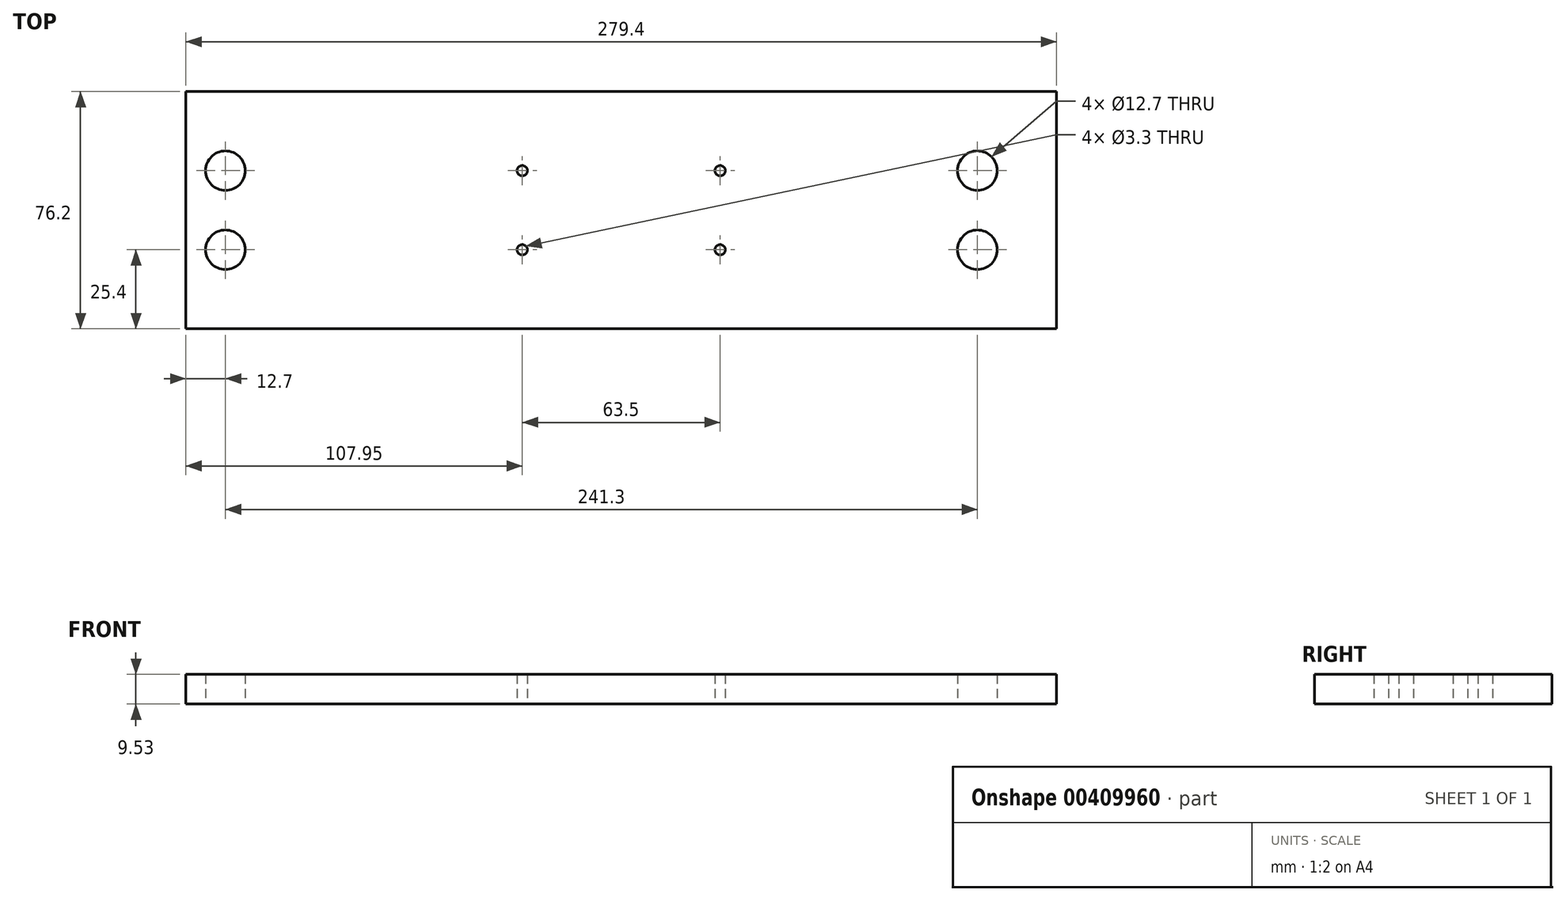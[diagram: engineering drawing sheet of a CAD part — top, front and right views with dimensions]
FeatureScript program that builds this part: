
annotation { "Feature Type Name" : "Feature", "Feature Type Description" : "" }
export const myFeature = defineFeature(function(context is Context, id is Id, definition is map)
    precondition{}
    {
        {
            var Q0;
            Q0=qCreatedBy(makeId("Top.planeOp"),FACE);
            var sketch = newSketch(context, id + "F0", { "sketchPlane" : qUnion([Q0])});
            skLineSegment(sketch, "E0.bottom", {"start": v(0, 0) * mm, "end": v(279.4, 0) * mm});
            skLineSegment(sketch, "E0.top", {"start": v(0, 76.2) * mm, "end": v(279.4, 76.2) * mm});
            skLineSegment(sketch, "E0.left", {"start": v(0, 0) * mm, "end": v(0, 76.2) * mm});
            skLineSegment(sketch, "E0.right", {"start": v(279.4, 0) * mm, "end": v(279.4, 76.2) * mm});
            skLineSegment(sketch, "E1", {"start": v(-6.57, 38.1) * mm, "end": v(295.71, 38.1) * mm, "construction": true});
            skPoint(sketch, "E1.startSnap0", {"position": v(0, 38.1) * mm});
            skCircle(sketch, "E2", {"center": v(12.7, 50.8) * mm, "radius": 6.35 * mm});
            skCircle(sketch, "E3", {"center": v(107.95, 50.8) * mm, "radius": 1.65 * mm});
            skCircle(sketch, "E4", {"center": v(171.45, 50.8) * mm, "radius": 1.65 * mm});
            skCircle(sketch, "E5", {"center": v(254, 50.8) * mm, "radius": 6.35 * mm});
            skCircle(sketch, "E6.MirrorC", {"center": v(12.7, 25.4) * mm, "radius": 6.35 * mm});
            skCircle(sketch, "E7.MirrorC", {"center": v(107.95, 25.4) * mm, "radius": 1.65 * mm});
            skCircle(sketch, "E8.MirrorC", {"center": v(254, 25.4) * mm, "radius": 6.35 * mm});
            skCircle(sketch, "E9.MirrorC", {"center": v(171.45, 25.4) * mm, "radius": 1.65 * mm});
            skSolve(sketch);
        }
        {
            var Q0;
            Q0=makeQuery(id+"F0.imprint","IMPRINT",FACE,{"disambiguationData":[TD([[makeQuery(id+"F0.imprint","IMPRINT",EDGE,{"derivedFrom":sQuery(id+"F0.wireOp",EDGE,"E0.bottom")}),1.0]])]});
            extrude(context, id + "F1", {"entities" : qUnion([Q0]), "depth" : 9.52 * mm});
        }
    });
